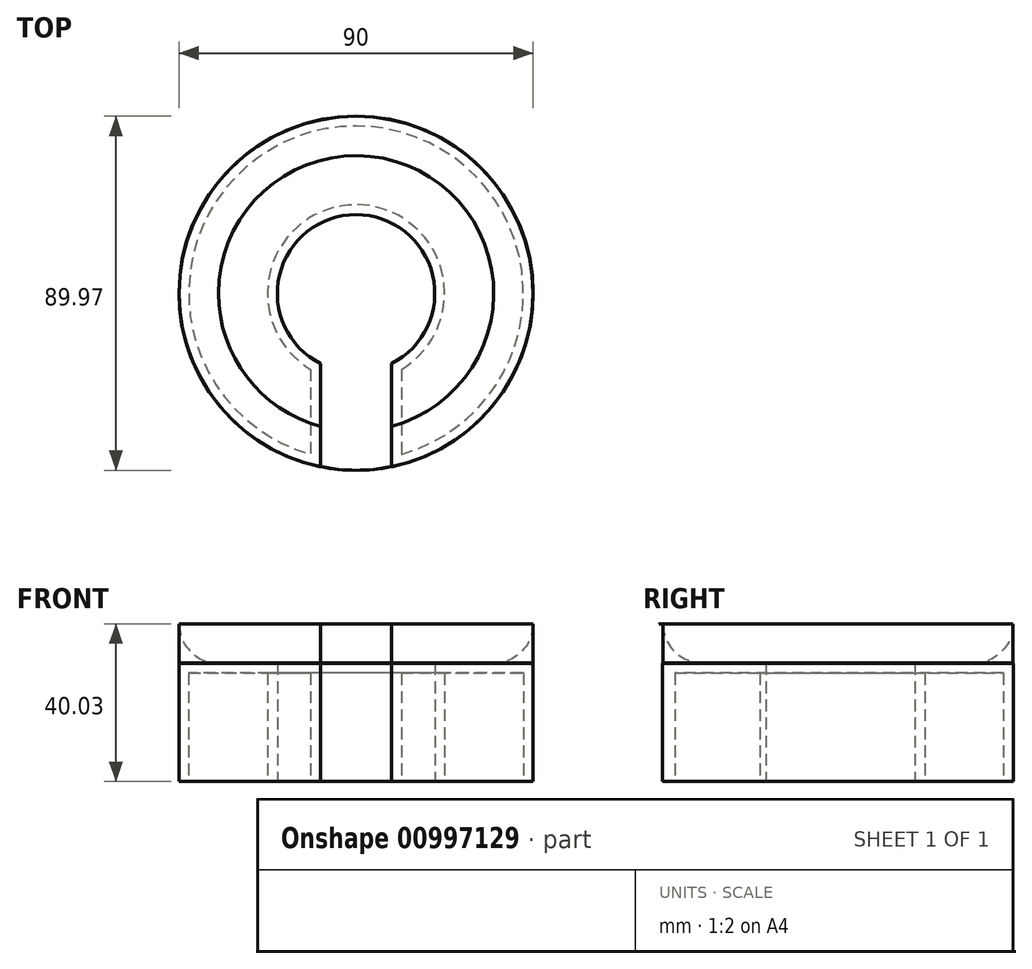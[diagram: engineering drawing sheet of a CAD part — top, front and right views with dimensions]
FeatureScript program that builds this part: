
annotation { "Feature Type Name" : "Feature", "Feature Type Description" : "" }
export const myFeature = defineFeature(function(context is Context, id is Id, definition is map)
    precondition{}
    {
        {
            var Q0;
            Q0=qCreatedBy(makeId("Top.planeOp"),FACE);
            var sketch = newSketch(context, id + "F0", { "sketchPlane" : qUnion([Q0])});
            skCircle(sketch, "E0", {"center": v(0, 0) * mm, "radius": 45 * mm});
            skSolve(sketch);
        }
        {
            var Q0;
            Q0=qCreatedBy(makeId("Top.planeOp"),FACE);
            var sketch = newSketch(context, id + "F1", { "sketchPlane" : qUnion([Q0])});
            skCircle(sketch, "E1", {"center": v(0, 0) * mm, "radius": 20 * mm});
            skSolve(sketch);
        }
        {
            var Q0;
            Q0=makeQuery(id+"F0.imprint","IMPRINT",FACE,{"disambiguationData":[TD([[makeQuery(id+"F0.imprint","IMPRINT",EDGE,{"derivedFrom":sQuery(id+"F0.wireOp",EDGE,"E0")}),1.0]])]});
            extrude(context, id + "F2", {"entities" : qUnion([Q0]), "depth" : 30 * mm, "offsetDistance" : 25 * mm});
        }
        {
            var Q0;
            Q0 = qSketchRegion(id + "F1", true);
            extrude(context, id + "F3", {"entities" : qUnion([Q0]), "depth" : 40 * mm, "offsetDistance" : 25 * mm});
        }
        {
            var Q0;
            Q0=makeQuery(id+"F3.opExtrude","SWEPT_BODY",BODY,{"disambiguationData":[OSD([sQuery(id+"F1.wireOp",EDGE,"E1")])]});
            var Q1;
            Q1=makeQuery(id+"F2.opExtrude","SWEPT_BODY",BODY,{"disambiguationData":[OSD([sQuery(id+"F0.wireOp",EDGE,"E0")])]});
            booleanBodies(context, id + "F4", {"operationType" : BooleanOperationType.SUBTRACTION, "tools" : qUnion([Q0]), "targets" : qUnion([Q1])});
        }
        {
            var Q0;
            Q0=qCreatedBy(makeId("Front.planeOp"),FACE);
            var sketch = newSketch(context, id + "F5", { "sketchPlane" : qUnion([Q0])});
            skLineSegment(sketch, "E2", {"start": v(-44.97, 40.03) * mm, "end": v(-44.97, 50.03) * mm});
            skArc(sketch, "E3", {"start": v(-44.97, 50.03) * mm, "mid": v(-42.04, 42.96) * mm, "end": v(-34.97, 40.03) * mm});
            skLineSegment(sketch, "E4", {"start": v(-44.97, 40.03) * mm, "end": v(-34.97, 40.03) * mm});
            skSolve(sketch);
        }
        {
            var Q0;
            Q0=qCreatedBy(makeId("Top.planeOp"),FACE);
            var sketch = newSketch(context, id + "F6", { "sketchPlane" : qUnion([Q0])});
            skCircle(sketch, "E5", {"center": v(0, 0) * mm, "radius": 45 * mm});
            skSolve(sketch);
        }
        {
            var Q0;
            Q0=makeQuery(id+"F5.imprint","IMPRINT",FACE,{"disambiguationData":[TD([[makeQuery(id+"F5.imprint","IMPRINT",EDGE,{"derivedFrom":sQuery(id+"F5.wireOp",EDGE,"E2")}),-1.0]])]});
            var Q1;
            Q1=sQuery(id+"F6.wireOp",EDGE,"E5");
            revolve(context, id + "F7", {"surfaceOperationType" : NewSurfaceOperationType.NEW, "entities" : qUnion([Q0]), "axis" : qUnion([Q1]), "revolveType" : RevolveType.FULL});
        }
        {
            var Q0;
            Q0=makeQuery(id+"F7.opRevolve","SWEPT_BODY",BODY,{"disambiguationData":[OSD([sQuery(id+"F5.wireOp",EDGE,"E2"),sQuery(id+"F5.wireOp",EDGE,"E3"),sQuery(id+"F5.wireOp",EDGE,"E4")])]});
            var Q1;
            Q1=makeQuery(id+"F2.opExtrude","SWEPT_FACE",FACE,{"disambiguationData":[OSD([sQuery(id+"F0.wireOp",EDGE,"E0")])]});
            transform(context, id + "F8", {"entities" : qUnion([Q0]), "transformType" : TransformType.TRANSLATION_DISTANCE, "transformDirection" : qUnion([Q1]), "distance" : 10 * mm, "makeCopy" : false});
        }
        {
            var Q0;
            Q0=qCreatedBy(makeId("Top.planeOp"),FACE);
            var sketch = newSketch(context, id + "F9", { "sketchPlane" : qUnion([Q0])});
            skLineSegment(sketch, "E6.bottom", {"start": v(9, -13.65) * mm, "end": v(-9, -13.65) * mm});
            skLineSegment(sketch, "E6.top", {"start": v(9, -71.7) * mm, "end": v(-9, -71.7) * mm});
            skLineSegment(sketch, "E6.left", {"start": v(9, -13.65) * mm, "end": v(9, -71.7) * mm});
            skLineSegment(sketch, "E6.right", {"start": v(-9, -13.65) * mm, "end": v(-9, -71.7) * mm});
            skPoint(sketch, "E6.middle", {"position": v(0, -42.68) * mm});
            skSolve(sketch);
        }
        {
            var Q0;
            Q0=makeQuery(id+"F9.imprint","IMPRINT",FACE,{"disambiguationData":[TD([[makeQuery(id+"F9.imprint","IMPRINT",EDGE,{"derivedFrom":sQuery(id+"F9.wireOp",EDGE,"E6.bottom")}),1.0]])]});
            extrude(context, id + "F10", {"entities" : qUnion([Q0]), "operationType" : NewBodyOperationType.REMOVE, "depth" : 40 * mm, "offsetDistance" : 25 * mm});
        }
        {
            var Q0;
            Q0=makeQuery(id+"F2.opExtrude","CAP_FACE",FACE,{"disambiguationData":[OSD([sQuery(id+"F0.wireOp",EDGE,"E0")])],"isStart":true});
            shell(context, id + "F11", {"entities" : qUnion([Q0]), "thickness" : 2.5 * mm});
        }
    });
